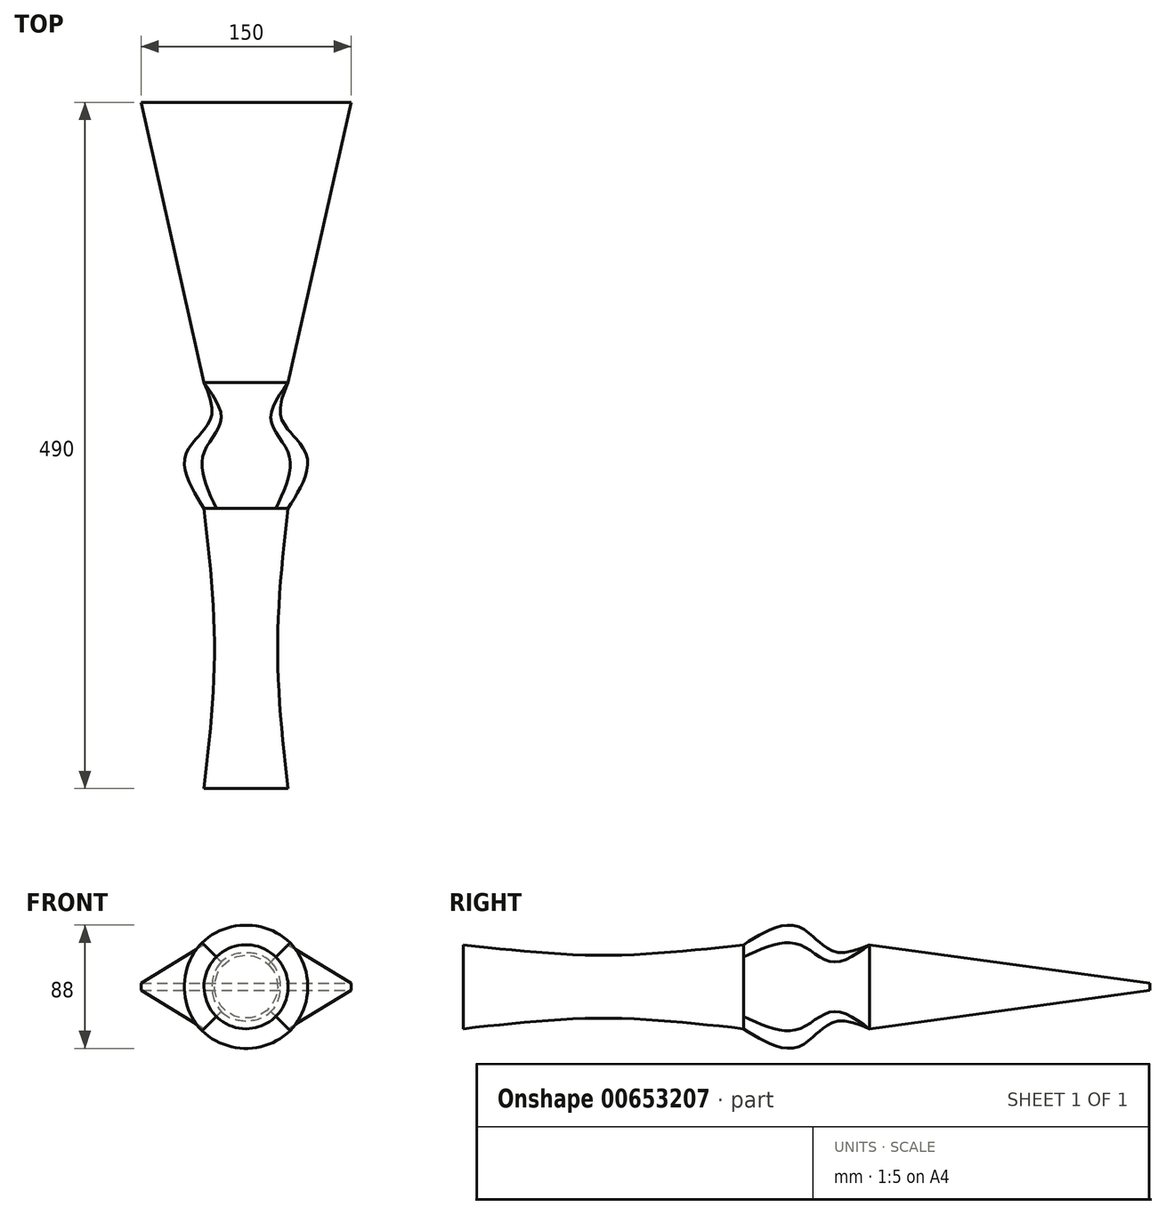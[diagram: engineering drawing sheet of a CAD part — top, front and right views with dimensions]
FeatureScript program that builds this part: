
annotation { "Feature Type Name" : "Feature", "Feature Type Description" : "" }
export const myFeature = defineFeature(function(context is Context, id is Id, definition is map)
    precondition{}
    {
        {
            var Q0;
            Q0=qCreatedBy(makeId("Front.planeOp"),FACE);
            cPlane(context, id + "F0", {"entities" : qUnion([Q0]), "cplaneType" : CPlaneType.OFFSET, "offset" : 25 * mm, "width" : 150 * mm, "height" : 150 * mm});
        }
        {
            var Q0;
            Q0=qCreatedBy(id+"F0.planeOp",FACE);
            cPlane(context, id + "F1", {"entities" : qUnion([Q0]), "cplaneType" : CPlaneType.OFFSET, "offset" : 25 * mm, "width" : 150 * mm, "height" : 150 * mm});
        }
        {
            var Q0;
            Q0=qCreatedBy(id+"F1.planeOp",FACE);
            cPlane(context, id + "F2", {"entities" : qUnion([Q0]), "cplaneType" : CPlaneType.OFFSET, "offset" : 40 * mm, "width" : 150 * mm, "height" : 150 * mm});
        }
        {
            var Q0;
            Q0=qCreatedBy(makeId("Front.planeOp"),FACE);
            var sketch = newSketch(context, id + "F3", { "sketchPlane" : qUnion([Q0])});
            skLineSegment(sketch, "E0.bottom", {"start": v(30, -30) * mm, "end": v(-30, -30) * mm});
            skLineSegment(sketch, "E0.top", {"start": v(30, 30) * mm, "end": v(-30, 30) * mm});
            skLineSegment(sketch, "E0.left", {"start": v(30, -30) * mm, "end": v(30, 30) * mm});
            skLineSegment(sketch, "E0.right", {"start": v(-30, -30) * mm, "end": v(-30, 30) * mm});
            skPoint(sketch, "E0.middle", {"position": v(0, 0) * mm});
            skSolve(sketch);
        }
        {
            var Q0;
            Q0=qCreatedBy(id+"F0.planeOp",FACE);
            var sketch = newSketch(context, id + "F4", { "sketchPlane" : qUnion([Q0])});
            skCircle(sketch, "E1", {"center": v(0, 0) * mm, "radius": 25 * mm});
            skSolve(sketch);
        }
        {
            var Q0;
            Q0=qCreatedBy(id+"F1.planeOp",FACE);
            var sketch = newSketch(context, id + "F5", { "sketchPlane" : qUnion([Q0])});
            skCircle(sketch, "E2", {"center": v(0, 0) * mm, "radius": 42.5 * mm});
            skSolve(sketch);
        }
        {
            var Q0;
            Q0=qCreatedBy(id+"F2.planeOp",FACE);
            var sketch = newSketch(context, id + "F6", { "sketchPlane" : qUnion([Q0])});
            skCircle(sketch, "E3", {"center": v(0, 0) * mm, "radius": 30 * mm});
            skSolve(sketch);
        }
        {
            var Q0;
            Q0=makeQuery(id+"F6.imprint","IMPRINT",FACE,{"disambiguationData":[TD([[makeQuery(id+"F6.imprint","IMPRINT",EDGE,{"derivedFrom":sQuery(id+"F6.wireOp",EDGE,"E3")}),1.0]])]});
            var Q1;
            Q1=makeQuery(id+"F5.imprint","IMPRINT",FACE,{"disambiguationData":[TD([[makeQuery(id+"F5.imprint","IMPRINT",EDGE,{"derivedFrom":sQuery(id+"F5.wireOp",EDGE,"E2")}),1.0]])]});
            var Q2;
            Q2=makeQuery(id+"F4.imprint","IMPRINT",FACE,{"disambiguationData":[TD([[makeQuery(id+"F4.imprint","IMPRINT",EDGE,{"derivedFrom":sQuery(id+"F4.wireOp",EDGE,"E1")}),1.0]])]});
            var Q3;
            Q3=makeQuery(id+"F3.imprint","IMPRINT",FACE,{"disambiguationData":[TD([[makeQuery(id+"F3.imprint","IMPRINT",EDGE,{"derivedFrom":sQuery(id+"F3.wireOp",EDGE,"E0.bottom")}),-1.0]])]});
            var Q4;
            Q4=makeQuery(id+"F6.imprint","IMPRINT",FACE,{"disambiguationData":[TD([[makeQuery(id+"F6.imprint","IMPRINT",EDGE,{"derivedFrom":sQuery(id+"F6.wireOp",EDGE,"E3")}),1.0]])]});
            loft(context, id + "F7", {"sheetProfilesArray" : [{ "sheetProfileEntities" : qUnion([Q0]) }, { "sheetProfileEntities" : qUnion([Q1]) }, { "sheetProfileEntities" : qUnion([Q2]) }, { "sheetProfileEntities" : qUnion([Q3]) }], "wireProfilesArray" : [{ "wireProfileEntities" : qUnion([Q4]) }]});
        }
        {
            var Q0;
            Q0=qCreatedBy(makeId("Front.planeOp"),FACE);
            cPlane(context, id + "F8", {"entities" : qUnion([Q0]), "cplaneType" : CPlaneType.OFFSET, "offset" : 200 * mm, "oppositeDirection" : true, "width" : 150 * mm, "height" : 150 * mm});
        }
        {
            var Q0;
            Q0=qCreatedBy(id+"F8.planeOp",FACE);
            var sketch = newSketch(context, id + "F9", { "sketchPlane" : qUnion([Q0])});
            skLineSegment(sketch, "E4.bottom", {"start": v(-75, -2.5) * mm, "end": v(75, -2.5) * mm});
            skLineSegment(sketch, "E4.top", {"start": v(-75, 2.5) * mm, "end": v(75, 2.5) * mm});
            skLineSegment(sketch, "E4.left", {"start": v(-75, -2.5) * mm, "end": v(-75, 2.5) * mm});
            skLineSegment(sketch, "E4.right", {"start": v(75, -2.5) * mm, "end": v(75, 2.5) * mm});
            skPoint(sketch, "E4.middle", {"position": v(0, 0) * mm});
            skSolve(sketch);
        }
        {
            var Q1;
            Q1=makeQuery(id+"F7.opLoft","CAP_FACE",FACE,{"disambiguationData":[OSD([makeQuery(id+"F3.imprint","IMPRINT",FACE,{"disambiguationData":[TD([[makeQuery(id+"F3.imprint","IMPRINT",EDGE,{"derivedFrom":sQuery(id+"F3.wireOp",EDGE,"E0.bottom")}),-1.0]])]})])],"isStart":true});
            var Q2;
            Q2=makeQuery(id+"F9.imprint","IMPRINT",FACE,{"disambiguationData":[TD([[makeQuery(id+"F9.imprint","IMPRINT",EDGE,{"derivedFrom":sQuery(id+"F9.wireOp",EDGE,"E4.bottom")}),1.0]])]});
            loft(context, id + "F10", {"operationType" : NewBodyOperationType.ADD, "sheetProfilesArray" : [{ "sheetProfileEntities" : qUnion([Q1]) }, { "sheetProfileEntities" : qUnion([Q2]) }]});
        }
        {
            var Q0;
            Q0=qCreatedBy(id+"F2.planeOp",FACE);
            var Q1;
            Q1 = qBodyType(qCreatedBy(id + "F12" ,EDGE), BodyType.WIRE);
            cPlane(context, id + "F11", {"entities" : qUnion([Q0, Q1]), "cplaneType" : CPlaneType.OFFSET, "offset" : 100 * mm, "width" : 150 * mm, "height" : 150 * mm});
        }
        {
            var Q0;
            Q0=qCreatedBy(id+"F11.planeOp",FACE);
            var sketch = newSketch(context, id + "F12", { "sketchPlane" : qUnion([Q0])});
            skCircle(sketch, "E5", {"center": v(0, 0) * mm, "radius": 22.5 * mm});
            skSolve(sketch);
        }
        {
            var Q0;
            Q0=qCreatedBy(id+"F11.planeOp",FACE);
            cPlane(context, id + "F13", {"entities" : qUnion([Q0]), "cplaneType" : CPlaneType.OFFSET, "offset" : 100 * mm, "width" : 150 * mm, "height" : 150 * mm});
        }
        {
            var Q0;
            Q0=qCreatedBy(id+"F13.planeOp",FACE);
            var sketch = newSketch(context, id + "F14", { "sketchPlane" : qUnion([Q0])});
            skCircle(sketch, "E6", {"center": v(0, 0) * mm, "radius": 30 * mm});
            skSolve(sketch);
        }
        {
            var Q0;
            Q0=makeQuery(id+"F6.imprint","IMPRINT",FACE,{"disambiguationData":[TD([[makeQuery(id+"F6.imprint","IMPRINT",EDGE,{"derivedFrom":sQuery(id+"F6.wireOp",EDGE,"E3")}),1.0]])]});
            var Q1;
            Q1=makeQuery(id+"F12.imprint","IMPRINT",FACE,{"disambiguationData":[TD([[makeQuery(id+"F12.imprint","IMPRINT",EDGE,{"derivedFrom":sQuery(id+"F12.wireOp",EDGE,"E5")}),1.0]])]});
            var Q2;
            Q2=makeQuery(id+"F14.imprint","IMPRINT",FACE,{"disambiguationData":[TD([[makeQuery(id+"F14.imprint","IMPRINT",EDGE,{"derivedFrom":sQuery(id+"F14.wireOp",EDGE,"E6")}),1.0]])]});
            loft(context, id + "F15", {"operationType" : NewBodyOperationType.ADD, "sheetProfilesArray" : [{ "sheetProfileEntities" : qUnion([Q0]) }, { "sheetProfileEntities" : qUnion([Q1]) }, { "sheetProfileEntities" : qUnion([Q2]) }]});
        }
    });
